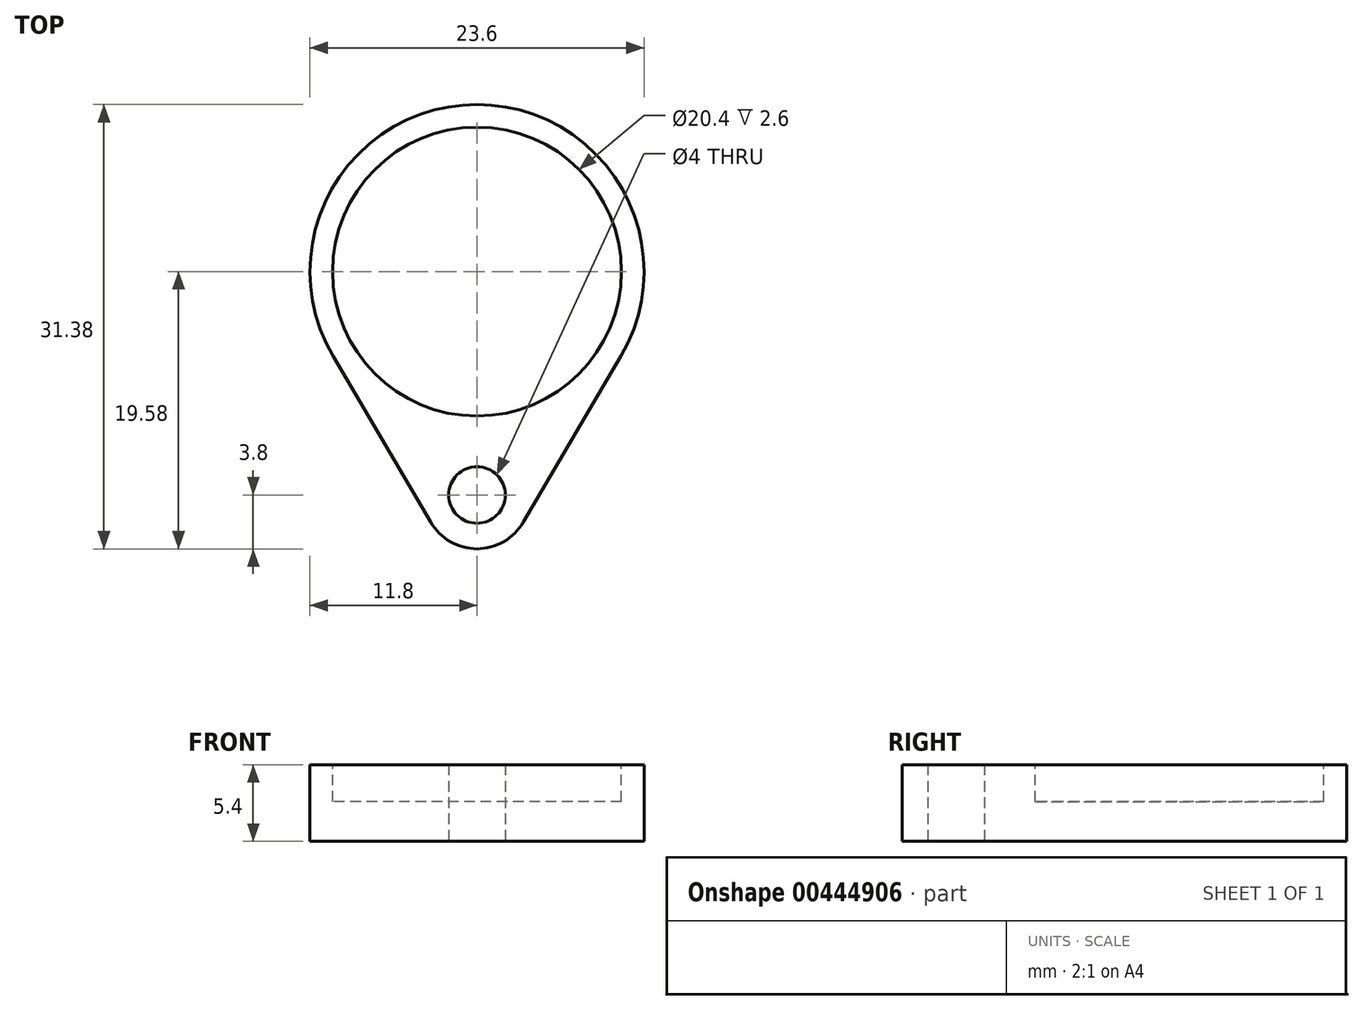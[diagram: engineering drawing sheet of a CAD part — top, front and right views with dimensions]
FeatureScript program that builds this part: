
annotation { "Feature Type Name" : "Feature", "Feature Type Description" : "" }
export const myFeature = defineFeature(function(context is Context, id is Id, definition is map)
    precondition{}
    {
        {
            var Q0;
            Q0=qCreatedBy(makeId("Top.planeOp"),FACE);
            var sketch = newSketch(context, id + "F0", { "sketchPlane" : qUnion([Q0])});
            skCircle(sketch, "E0", {"center": v(0, 0) * mm, "radius": 10 * mm});
            skSolve(sketch);
        }
        {
            var Q0;
            Q0=qSketchRegion(id+"F0",true);
            extrude(context, id + "F1", {"entities" : qUnion([Q0]), "depth" : 1 * mm});
        }
        {
            var Q0;
            Q0=makeQuery(id+"F1.opExtrude","CAP_FACE",FACE,{"disambiguationData":[OSD([sQuery(id+"F0.wireOp",EDGE,"E0")])],"isStart":true});
            var sketch = newSketch(context, id + "F2", { "sketchPlane" : qUnion([Q0])});
            skCircle(sketch, "E1", {"center": v(0, 0) * mm, "radius": 11.8 * mm});
            skSolve(sketch);
        }
        {
            var Q0;
            Q0=qSketchRegion(id+"F2",true);
            extrude(context, id + "F3", {"entities" : qUnion([Q0]), "depth" : 1 * mm});
        }
        {
            var Q0;
            Q0=makeQuery(id+"F3.opExtrude","CAP_FACE",FACE,{"disambiguationData":[OSD([sQuery(id+"F2.wireOp",EDGE,"E1")])],"isStart":true});
            var sketch = newSketch(context, id + "F4", { "sketchPlane" : qUnion([Q0])});
            skCircle(sketch, "E2.0", {"center": v(0, 0) * mm, "radius": 11.8 * mm});
            skCircle(sketch, "E3", {"center": v(0, 0) * mm, "radius": 10 * mm});
            skSolve(sketch);
        }
        {
            var Q0;
            Q0=qSketchRegion(id+"F4",true);
            extrude(context, id + "F5", {"entities" : qUnion([Q0]), "operationType" : NewBodyOperationType.ADD, "depth" : 1 * mm});
        }
        {
            var Q0;
            Q0=makeQuery(id+"F5.opExtrude","CAP_FACE",FACE,{"disambiguationData":[OSD([sQuery(id+"F4.wireOp",EDGE,"E2.0"),sQuery(id+"F4.wireOp",EDGE,"E3")])],"isStart":false});
            var sketch = newSketch(context, id + "F6", { "sketchPlane" : qUnion([Q0])});
            skCircle(sketch, "E4.0.0", {"center": v(0, 0) * mm, "radius": 11.8 * mm});
            skSolve(sketch);
        }
        {
            var Q0;
            Q0=qSketchRegion(id+"F6",true);
            extrude(context, id + "F7", {"entities" : qUnion([Q0]), "operationType" : NewBodyOperationType.ADD, "depth" : 3.4 * mm});
        }
        {
            var Q0;
            Q0=makeQuery(id+"F7.opExtrude","CAP_FACE",FACE,{"disambiguationData":[OSD([sQuery(id+"F6.wireOp",EDGE,"E4.0.0")])],"isStart":false});
            var sketch = newSketch(context, id + "F8", { "sketchPlane" : qUnion([Q0])});
            skCircle(sketch, "E5", {"center": v(0, 0) * mm, "radius": 10.2 * mm});
            skSolve(sketch);
        }
        {
            var Q0;
            Q0=qSketchRegion(id+"F8",true);
            extrude(context, id + "F9", {"entities" : qUnion([Q0]), "operationType" : NewBodyOperationType.REMOVE, "oppositeDirection" : true, "depth" : 2.6 * mm});
        }
        {
            var Q0;
            Q0=makeQuery(id+"F3.opExtrude","CAP_FACE",FACE,{"disambiguationData":[OSD([sQuery(id+"F2.wireOp",EDGE,"E1")])],"isStart":false});
            var sketch = newSketch(context, id + "F10", { "sketchPlane" : qUnion([Q0])});
            skCircle(sketch, "E6", {"center": v(0, 15.78) * mm, "radius": 2 * mm});
            skCircle(sketch, "E7", {"center": v(0, 15.78) * mm, "radius": 3.8 * mm});
            skLineSegment(sketch, "E8", {"start": v(-3.28, 17.7) * mm, "end": v(-10.17, 5.98) * mm});
            skLineSegment(sketch, "E9", {"start": v(3.28, 17.7) * mm, "end": v(10.17, 5.98) * mm});
            skSolve(sketch);
        }
        {
            var Q0;
            Q0 = qSketchRegion(id + "F10", true);
            var Q1;
            {var subQ0=sQuery(id+"F10.wireOp",EDGE,"E8");Q1=makeQuery(id+"F10.imprint","IMPRINT",FACE,{"disambiguationData":[TD([[makeQuery(id+"F10.imprint","IMPRINT",EDGE,{"derivedFrom":subQ0}),1.0]])]});}
            var Q2;
            Q2=makeQuery(id+"F7.opExtrude","CAP_FACE",FACE,{"disambiguationData":[OSD([sQuery(id+"F6.wireOp",EDGE,"E4.0.0")])],"isStart":false});
            extrude(context, id + "F11", {"entities" : qUnion([Q0, Q1]), "operationType" : NewBodyOperationType.ADD, "endBound" : BoundingType.UP_TO_SURFACE, "oppositeDirection" : true, "endBoundEntityFace" : qUnion([Q2]), "depth" : 4 * mm});
        }
    });
